# Revit family: Pendant Light - Linear - 2 Lamp
name_source: partatom
category: Lighting Fixtures
revit_build: Autodesk Revit Architecture 2012 (Build: 20110210_1515)
units: mm (PartAtom-declared; Revit-internal decimal feet)

## types (4) — shared parameters
Assembly Code = D5020210
Ballast Number of Poles = 1
Ceiling Mount Material = Metal - Paint Finish - Ivory, Glossy
Color Filter = 16777215
Diffuser Material = Glass - White, High Luminance
Dimming Lamp Color Temperature Shift = <None>
Emit Shape Visible in Rendering = No
Emit from Rectangle Width = 0' - 5"
Lamp = T-12
Light Casing Material = Metal - Paint Finish - Ivory, Glossy
Light Source Symbol Size = 2' - 0"
Load Classification = Lighting - Dwelling Unit

## per-type parameters (varying)
| type | Apparent Load | Ballast Voltage | Drop From Ceiling | Emit from Rectangle Length | Light Casing Length |
| 48" - 120V | 64 VA | 120 V | 2' - 0" | 3' - 8" | 4' - 0" |
| 48" - 277V | 64 VA | 277 V | 2' - 0" | 3' - 8" | 4' - 0" |
| 96" - 120V | 150 VA | 120 V | 1' - 0" | 7' - 8" | 8' - 0" |
| 96" - 277V | 150 VA | 277 V | 1' - 0" | 7' - 8" | 8' - 0" |

## geometry (parser evidence)
native form markers: Sweep x1
no freeform markers — native parametric forms only
